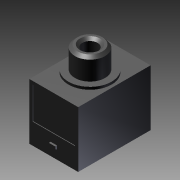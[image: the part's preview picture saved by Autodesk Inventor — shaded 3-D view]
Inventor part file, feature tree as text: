
AUTODESK INVENTOR PART (.ipt)
format: ipt  version: 2011 SP1 (Build 150282100, 282)  size: 144,384 bytes
history: native  units: in
note: dims shown in document units (in); Inventor stores cm internally (conversion verified against a paired STEP export)
features: sketch x10, extrude x8, revolve x1, hole x1
ambient origin geometry x8: Origin, YZ Plane, XZ Plane, XY Plane, X Axis, Y Axis, Z Axis, Center Point
bodies: Solid1 (feature_tree), body_to_body2_XY (feature_tree), body_to_body2_YZ (feature_tree), body_to_body2_ZX (feature_tree), body_to_body2_X (feature_tree), body_to_body2_Y (feature_tree), body_to_body2_Z (feature_tree), body_to_body2_Center (feature_tree), body_to_dummy_XY (feature_tree), body_to_dummy_YZ (feature_tree), body_to_dummy_ZX (feature_tree), body_to_dummy_X (feature_tree), body_to_dummy_Y (feature_tree), body_to_dummy_Z (feature_tree), body_to_dummy_Center (feature_tree), body_to_terminal_XY (feature_tree), body_to_terminal_YZ (feature_tree), body_to_terminal_ZX (feature_tree), body_to_terminal_X (feature_tree), body_to_terminal_Y (feature_tree), body_to_terminal_Z (feature_tree), body_to_terminal_Center (feature_tree), body_to_toggle_XY (feature_tree), body_to_toggle_YZ (feature_tree), body_to_toggle_ZX (feature_tree), body_to_toggle_X (feature_tree), body_to_toggle_Y (feature_tree), body_to_toggle_Z (feature_tree), body_to_toggle_Center (feature_tree), body_to_washer_XY (feature_tree), body_to_washer_YZ (feature_tree), body_to_washer_ZX (feature_tree), body_to_washer_X (feature_tree), body_to_washer_Y (feature_tree), body_to_washer_Z (feature_tree), body_to_washer_Center (feature_tree)
feature tree (20):
  extrude  "Extrusion1"  Depth=0.039in TaperAngle=0.0deg
  extrude  "Extrusion2"  Depth=0.339in TaperAngle=0.0deg
  revolve  "Revolution1"  [1 undecoded]
  extrude  "Extrusion3"  Depth=0.01in TaperAngle=0.0deg
  hole  "Drilling 1"  [1 undecoded]
  extrude  "Extrusion4"  [1 undecoded]
  extrude  "Extrusion5"  [1 undecoded]
  extrude  "Extrusion6"  [1 undecoded]
  extrude  "Extrusion7"  [1 undecoded]
  extrude  "Extrusion8"  [1 undecoded]
  sketch  "Sketch_1"  dims[d0=0.878in d1=0.0in d2=0.039in d3=0.0in]
  sketch  "Sketch_2"  dims[d4=360.0deg d5=0.339in d6=0.0in]
  sketch  "Sketch_3"  dims[d7=0.2362in d8=0.75in d9=0.315in d10=0.25in d11=0.6184in d12=0.339in d13=0.0in d14=0.01in d15=0.0in]
  sketch  "Sketch_10"
  sketch  "Sketch5"  dims[d16=0.01in d17=0.0in d18=0.01in d19=0.0in]
  sketch  "Sketch_5"  dims[d20=0.1in d21=0.0in d22=0.1in d23=0.0in]
  sketch  "Sketch_6"
  sketch  "Sketch_7"
  sketch  "Sketch_8"
  sketch  "Sketch_9"
note: 7 required parameter values undecoded (feature->parameter linkage not recoverable at this tier; creation-order binding heuristic only, values carry confidence <= 0.55)